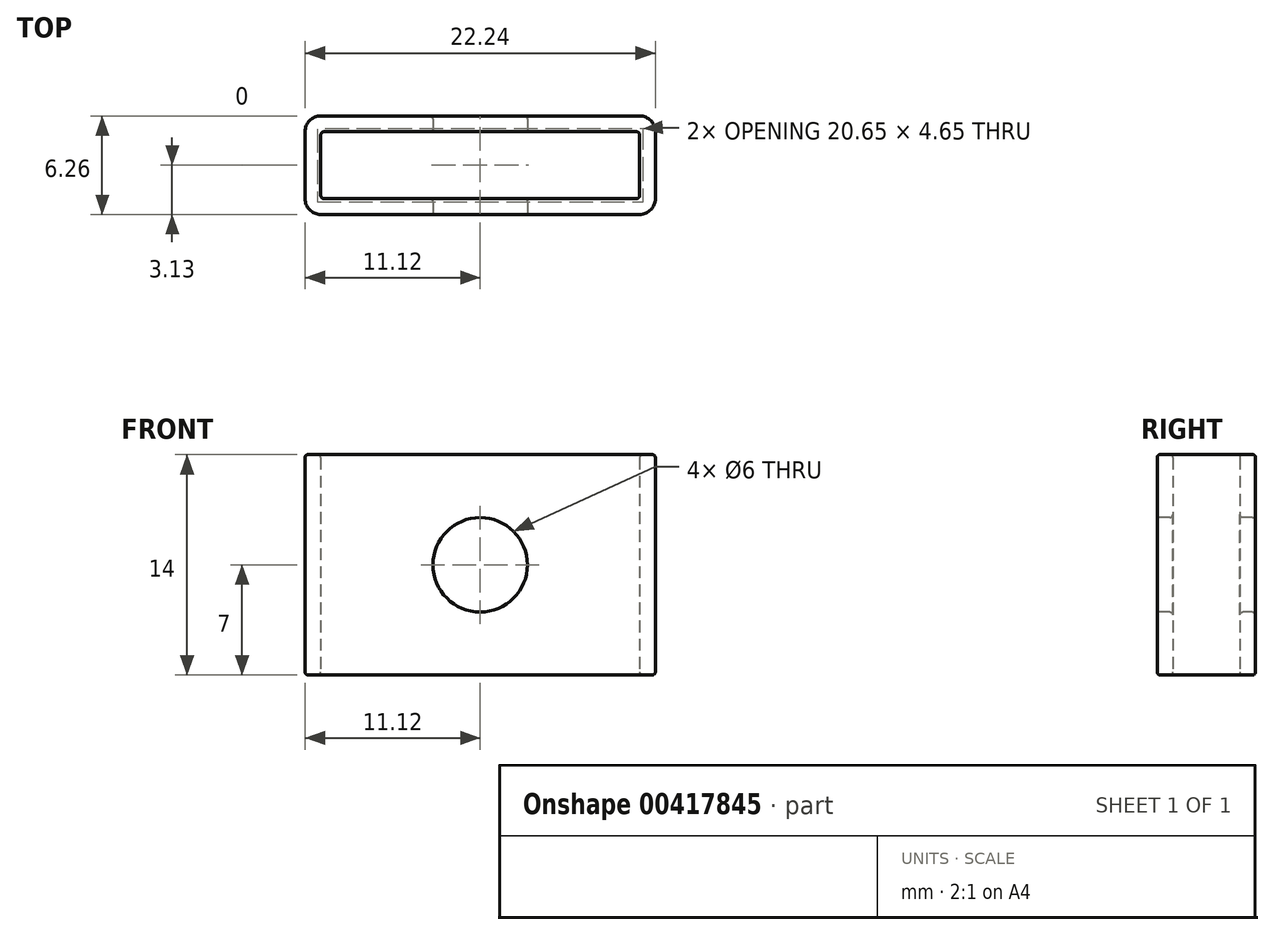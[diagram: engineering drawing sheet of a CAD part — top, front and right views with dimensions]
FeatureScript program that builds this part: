
annotation { "Feature Type Name" : "Feature", "Feature Type Description" : "" }
export const myFeature = defineFeature(function(context is Context, id is Id, definition is map)
    precondition{}
    {
        {
            var Q0;
            Q0=qCreatedBy(makeId("Top.planeOp"),FACE);
            var sketch = newSketch(context, id + "F0", { "sketchPlane" : qUnion([Q0])});
            skLineSegment(sketch, "E0.bottom", {"start": v(10.12, -2.12) * mm, "end": v(-10.12, -2.13) * mm});
            skLineSegment(sketch, "E0.top", {"start": v(10.12, 2.13) * mm, "end": v(-10.12, 2.12) * mm});
            skLineSegment(sketch, "E0.left", {"start": v(10.12, -2.12) * mm, "end": v(10.12, 2.13) * mm});
            skLineSegment(sketch, "E0.right", {"start": v(-10.12, -2.13) * mm, "end": v(-10.12, 2.12) * mm});
            skPoint(sketch, "E0.middle", {"position": v(0, 0) * mm});
            skLineSegment(sketch, "E1.0", {"start": v(11.12, 3.13) * mm, "end": v(-11.12, 3.12) * mm});
            skLineSegment(sketch, "E1.1", {"start": v(11.12, -3.12) * mm, "end": v(11.12, 3.13) * mm});
            skLineSegment(sketch, "E1.2", {"start": v(11.12, -3.12) * mm, "end": v(-11.12, -3.13) * mm});
            skLineSegment(sketch, "E1.3", {"start": v(-11.12, -3.13) * mm, "end": v(-11.12, 3.12) * mm});
            skSolve(sketch);
        }
        {
            var Q0;
            Q0=makeQuery(id+"F0.imprint","IMPRINT",FACE,{"disambiguationData":[TD([[makeQuery(id+"F0.imprint","IMPRINT",EDGE,{"derivedFrom":sQuery(id+"F0.wireOp",EDGE,"E0.bottom")}),1.0]])]});
            extrude(context, id + "F1", {"entities" : qUnion([Q0]), "depth" : 14 * mm});
        }
        {
            var Q0;
            Q0=makeQuery(id+"F1.opExtrude","SWEPT_EDGE",EDGE,{"disambiguationData":[OSD([sQuery(id+"F0.wireOp",EDGE,"E1.2"),sQuery(id+"F0.wireOp",EDGE,"E1.3")])]});
            var Q1;
            Q1=makeQuery(id+"F1.opExtrude","SWEPT_EDGE",EDGE,{"disambiguationData":[OSD([sQuery(id+"F0.wireOp",EDGE,"E1.0"),sQuery(id+"F0.wireOp",EDGE,"E1.3")])]});
            var Q2;
            Q2=makeQuery(id+"F1.opExtrude","SWEPT_EDGE",EDGE,{"disambiguationData":[OSD([sQuery(id+"F0.wireOp",EDGE,"E1.0"),sQuery(id+"F0.wireOp",EDGE,"E1.1")])]});
            var Q3;
            Q3=makeQuery(id+"F1.opExtrude","SWEPT_EDGE",EDGE,{"disambiguationData":[OSD([sQuery(id+"F0.wireOp",EDGE,"E1.1"),sQuery(id+"F0.wireOp",EDGE,"E1.2")])]});
            fillet(context, id + "F2", {"entities" : qUnion([Q0, Q1, Q2, Q3]), "radius" : 1 * mm, "tangentPropagation" : true, "allowEdgeOverflow" : false});
        }
        {
            var Q0;
            Q0=makeQuery(id+"F1.opExtrude","SWEPT_EDGE",EDGE,{"disambiguationData":[OSD([sQuery(id+"F0.wireOp",EDGE,"E0.top"),sQuery(id+"F0.wireOp",EDGE,"E0.right")])]});
            var Q1;
            Q1=makeQuery(id+"F1.opExtrude","SWEPT_EDGE",EDGE,{"disambiguationData":[OSD([sQuery(id+"F0.wireOp",EDGE,"E0.bottom"),sQuery(id+"F0.wireOp",EDGE,"E0.right")])]});
            var Q2;
            Q2=makeQuery(id+"F1.opExtrude","SWEPT_EDGE",EDGE,{"disambiguationData":[OSD([sQuery(id+"F0.wireOp",EDGE,"E0.top"),sQuery(id+"F0.wireOp",EDGE,"E0.left")])]});
            var Q3;
            Q3=makeQuery(id+"F1.opExtrude","SWEPT_EDGE",EDGE,{"disambiguationData":[OSD([sQuery(id+"F0.wireOp",EDGE,"E0.bottom"),sQuery(id+"F0.wireOp",EDGE,"E0.left")])]});
            fillet(context, id + "F3", {"entities" : qUnion([Q0, Q1, Q2, Q3]), "radius" : .2 * mm, "tangentPropagation" : true, "allowEdgeOverflow" : false});
        }
        {
            var Q0;
            {var subQ0=sQuery(id+"F0.wireOp",EDGE,"E1.3");var subQ1=sQuery(id+"F0.wireOp",EDGE,"E1.2");Q0=makeQuery(id+"F2.opFillet","BLEND_EDGE",EDGE,{"blendedFrom":[makeQuery(id+"F1.opExtrude","SWEPT_EDGE",EDGE,{"disambiguationData":[OSD([subQ1,subQ0])]}),makeQuery(id+"F1.opExtrude","CAP_FACE",FACE,{"disambiguationData":[OSD([sQuery(id+"F0.wireOp",EDGE,"E0.bottom"),sQuery(id+"F0.wireOp",EDGE,"E0.top"),sQuery(id+"F0.wireOp",EDGE,"E0.left"),sQuery(id+"F0.wireOp",EDGE,"E0.right"),sQuery(id+"F0.wireOp",EDGE,"E1.0"),sQuery(id+"F0.wireOp",EDGE,"E1.1"),subQ1,subQ0])],"isStart":false})],"blendedInto":[makeQuery(id+"F1.opExtrude","CAP_FACE",FACE,{"disambiguationData":[OSD([sQuery(id+"F0.wireOp",EDGE,"E0.bottom"),sQuery(id+"F0.wireOp",EDGE,"E0.top"),sQuery(id+"F0.wireOp",EDGE,"E0.left"),sQuery(id+"F0.wireOp",EDGE,"E0.right"),sQuery(id+"F0.wireOp",EDGE,"E1.0"),sQuery(id+"F0.wireOp",EDGE,"E1.1"),subQ1,subQ0])],"isStart":false})]});}
            var Q1;
            {var subQ0=sQuery(id+"F0.wireOp",EDGE,"E0.right");var subQ1=sQuery(id+"F0.wireOp",EDGE,"E0.top");Q1=makeQuery(id+"F2.opFillet","BLEND_EDGE",EDGE,{"blendedFrom":[makeQuery(id+"F1.opExtrude","SWEPT_EDGE",EDGE,{"disambiguationData":[OSD([subQ1,subQ0])]}),makeQuery(id+"F1.opExtrude","CAP_FACE",FACE,{"disambiguationData":[OSD([sQuery(id+"F0.wireOp",EDGE,"E0.bottom"),subQ1,sQuery(id+"F0.wireOp",EDGE,"E0.left"),subQ0,sQuery(id+"F0.wireOp",EDGE,"E1.0"),sQuery(id+"F0.wireOp",EDGE,"E1.1"),sQuery(id+"F0.wireOp",EDGE,"E1.2"),sQuery(id+"F0.wireOp",EDGE,"E1.3")])],"isStart":false})],"blendedInto":[makeQuery(id+"F1.opExtrude","CAP_FACE",FACE,{"disambiguationData":[OSD([sQuery(id+"F0.wireOp",EDGE,"E0.bottom"),subQ1,sQuery(id+"F0.wireOp",EDGE,"E0.left"),subQ0,sQuery(id+"F0.wireOp",EDGE,"E1.0"),sQuery(id+"F0.wireOp",EDGE,"E1.1"),sQuery(id+"F0.wireOp",EDGE,"E1.2"),sQuery(id+"F0.wireOp",EDGE,"E1.3")])],"isStart":false})]});}
            var Q2;
            {var subQ0=sQuery(id+"F0.wireOp",EDGE,"E0.right");var subQ1=sQuery(id+"F0.wireOp",EDGE,"E0.bottom");Q2=makeQuery(id+"F2.opFillet","BLEND_EDGE",EDGE,{"blendedFrom":[makeQuery(id+"F1.opExtrude","SWEPT_EDGE",EDGE,{"disambiguationData":[OSD([subQ1,subQ0])]}),makeQuery(id+"F1.opExtrude","CAP_FACE",FACE,{"disambiguationData":[OSD([subQ1,sQuery(id+"F0.wireOp",EDGE,"E0.top"),sQuery(id+"F0.wireOp",EDGE,"E0.left"),subQ0,sQuery(id+"F0.wireOp",EDGE,"E1.0"),sQuery(id+"F0.wireOp",EDGE,"E1.1"),sQuery(id+"F0.wireOp",EDGE,"E1.2"),sQuery(id+"F0.wireOp",EDGE,"E1.3")])],"isStart":true})],"blendedInto":[makeQuery(id+"F1.opExtrude","CAP_FACE",FACE,{"disambiguationData":[OSD([subQ1,sQuery(id+"F0.wireOp",EDGE,"E0.top"),sQuery(id+"F0.wireOp",EDGE,"E0.left"),subQ0,sQuery(id+"F0.wireOp",EDGE,"E1.0"),sQuery(id+"F0.wireOp",EDGE,"E1.1"),sQuery(id+"F0.wireOp",EDGE,"E1.2"),sQuery(id+"F0.wireOp",EDGE,"E1.3")])],"isStart":true})]});}
            var Q3;
            {var subQ0=sQuery(id+"F0.wireOp",EDGE,"E1.3");var subQ1=sQuery(id+"F0.wireOp",EDGE,"E1.2");Q3=makeQuery(id+"F2.opFillet","BLEND_EDGE",EDGE,{"blendedFrom":[makeQuery(id+"F1.opExtrude","SWEPT_EDGE",EDGE,{"disambiguationData":[OSD([subQ1,subQ0])]}),makeQuery(id+"F1.opExtrude","CAP_FACE",FACE,{"disambiguationData":[OSD([sQuery(id+"F0.wireOp",EDGE,"E0.bottom"),sQuery(id+"F0.wireOp",EDGE,"E0.top"),sQuery(id+"F0.wireOp",EDGE,"E0.left"),sQuery(id+"F0.wireOp",EDGE,"E0.right"),sQuery(id+"F0.wireOp",EDGE,"E1.0"),sQuery(id+"F0.wireOp",EDGE,"E1.1"),subQ1,subQ0])],"isStart":true})],"blendedInto":[makeQuery(id+"F1.opExtrude","CAP_FACE",FACE,{"disambiguationData":[OSD([sQuery(id+"F0.wireOp",EDGE,"E0.bottom"),sQuery(id+"F0.wireOp",EDGE,"E0.top"),sQuery(id+"F0.wireOp",EDGE,"E0.left"),sQuery(id+"F0.wireOp",EDGE,"E0.right"),sQuery(id+"F0.wireOp",EDGE,"E1.0"),sQuery(id+"F0.wireOp",EDGE,"E1.1"),subQ1,subQ0])],"isStart":true})]});}
            var Q4;
            {var subQ0=sQuery(id+"F0.wireOp",EDGE,"E0.left");var subQ1=sQuery(id+"F0.wireOp",EDGE,"E0.bottom");Q4=makeQuery(id+"F3.opFillet","BLEND_EDGE",EDGE,{"blendedFrom":[makeQuery(id+"F1.opExtrude","SWEPT_EDGE",EDGE,{"disambiguationData":[OSD([subQ1,subQ0])]}),makeQuery(id+"F1.opExtrude","CAP_FACE",FACE,{"disambiguationData":[OSD([subQ1,sQuery(id+"F0.wireOp",EDGE,"E0.top"),subQ0,sQuery(id+"F0.wireOp",EDGE,"E0.right"),sQuery(id+"F0.wireOp",EDGE,"E1.0"),sQuery(id+"F0.wireOp",EDGE,"E1.1"),sQuery(id+"F0.wireOp",EDGE,"E1.2"),sQuery(id+"F0.wireOp",EDGE,"E1.3")])],"isStart":false})],"blendedInto":[makeQuery(id+"F1.opExtrude","CAP_FACE",FACE,{"disambiguationData":[OSD([subQ1,sQuery(id+"F0.wireOp",EDGE,"E0.top"),subQ0,sQuery(id+"F0.wireOp",EDGE,"E0.right"),sQuery(id+"F0.wireOp",EDGE,"E1.0"),sQuery(id+"F0.wireOp",EDGE,"E1.1"),sQuery(id+"F0.wireOp",EDGE,"E1.2"),sQuery(id+"F0.wireOp",EDGE,"E1.3")])],"isStart":false})]});}
            var Q5;
            {var subQ0=sQuery(id+"F0.wireOp",EDGE,"E0.left");var subQ1=sQuery(id+"F0.wireOp",EDGE,"E0.bottom");Q5=makeQuery(id+"F3.opFillet","BLEND_EDGE",EDGE,{"blendedFrom":[makeQuery(id+"F1.opExtrude","SWEPT_EDGE",EDGE,{"disambiguationData":[OSD([subQ1,subQ0])]}),makeQuery(id+"F1.opExtrude","CAP_FACE",FACE,{"disambiguationData":[OSD([subQ1,sQuery(id+"F0.wireOp",EDGE,"E0.top"),subQ0,sQuery(id+"F0.wireOp",EDGE,"E0.right"),sQuery(id+"F0.wireOp",EDGE,"E1.0"),sQuery(id+"F0.wireOp",EDGE,"E1.1"),sQuery(id+"F0.wireOp",EDGE,"E1.2"),sQuery(id+"F0.wireOp",EDGE,"E1.3")])],"isStart":true})],"blendedInto":[makeQuery(id+"F1.opExtrude","CAP_FACE",FACE,{"disambiguationData":[OSD([subQ1,sQuery(id+"F0.wireOp",EDGE,"E0.top"),subQ0,sQuery(id+"F0.wireOp",EDGE,"E0.right"),sQuery(id+"F0.wireOp",EDGE,"E1.0"),sQuery(id+"F0.wireOp",EDGE,"E1.1"),sQuery(id+"F0.wireOp",EDGE,"E1.2"),sQuery(id+"F0.wireOp",EDGE,"E1.3")])],"isStart":true})]});}
            fillet(context, id + "F4", {"entities" : qUnion([Q0, Q1, Q2, Q3, Q4, Q5]), "radius" : .2 * mm, "tangentPropagation" : true, "allowEdgeOverflow" : false});
        }
        {
            var Q0;
            Q0=makeQuery(id+"F1.opExtrude","SWEPT_FACE",FACE,{"disambiguationData":[OSD([sQuery(id+"F0.wireOp",EDGE,"E1.2")])]});
            var sketch = newSketch(context, id + "F5", { "sketchPlane" : qUnion([Q0])});
            skCircle(sketch, "E2", {"center": v(0, 7) * mm, "radius": 3 * mm});
            skPoint(sketch, "E2.centerSnap0", {"position": v(10.12, 7) * mm});
            skSolve(sketch);
        }
        {
            var Q0;
            Q0=makeQuery(id+"F5.imprint","IMPRINT",FACE,{"disambiguationData":[TD([[makeQuery(id+"F5.imprint","IMPRINT",EDGE,{"derivedFrom":sQuery(id+"F5.wireOp",EDGE,"E2")}),1.0]])]});
            extrude(context, id + "F6", {"entities" : qUnion([Q0]), "operationType" : NewBodyOperationType.REMOVE, "endBound" : BoundingType.THROUGH_ALL, "oppositeDirection" : true, "depth" : 25 * mm});
        }
        {
            var Q0;
            Q0=makeQuery(id+"F6.boolean.opBoolean","INTERSECT",EDGE,{"derivedFrom":[makeQuery(id+"F1.opExtrude","SWEPT_FACE",FACE,{"disambiguationData":[OSD([sQuery(id+"F0.wireOp",EDGE,"E1.0")])]}),makeQuery(id+"F6.opExtrude","SWEPT_FACE",FACE,{"disambiguationData":[OSD([sQuery(id+"F5.wireOp",EDGE,"E2")])]})]});
            var Q1;
            Q1=makeQuery(id+"F6.boolean.opBoolean","COPY",EDGE,{"derivedFrom":makeQuery(id+"F6.opExtrude","CAP_EDGE",EDGE,{"disambiguationData":[OSD([sQuery(id+"F5.wireOp",EDGE,"E2")])],"isStart":true})});
            var Q2;
            Q2=makeQuery(id+"F6.boolean.opBoolean","INTERSECT",EDGE,{"derivedFrom":[makeQuery(id+"F1.opExtrude","SWEPT_FACE",FACE,{"disambiguationData":[OSD([sQuery(id+"F0.wireOp",EDGE,"E0.bottom")])]}),makeQuery(id+"F6.opExtrude","SWEPT_FACE",FACE,{"disambiguationData":[OSD([sQuery(id+"F5.wireOp",EDGE,"E2")])]})]});
            var Q3;
            Q3=makeQuery(id+"F6.boolean.opBoolean","INTERSECT",EDGE,{"derivedFrom":[makeQuery(id+"F1.opExtrude","SWEPT_FACE",FACE,{"disambiguationData":[OSD([sQuery(id+"F0.wireOp",EDGE,"E0.top")])]}),makeQuery(id+"F6.opExtrude","SWEPT_FACE",FACE,{"disambiguationData":[OSD([sQuery(id+"F5.wireOp",EDGE,"E2")])]})]});
            fillet(context, id + "F7", {"entities" : qUnion([Q0, Q1, Q2, Q3]), "radius" : .2 * mm, "tangentPropagation" : true, "allowEdgeOverflow" : false});
        }
    });
